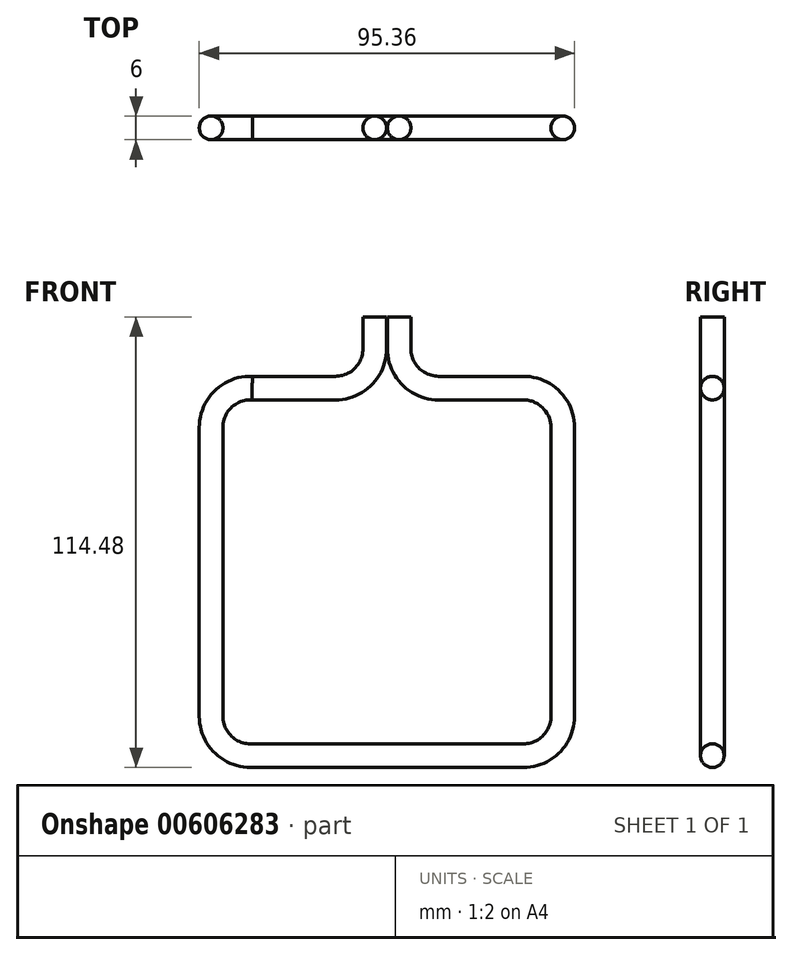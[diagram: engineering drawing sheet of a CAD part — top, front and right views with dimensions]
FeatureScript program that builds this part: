
annotation { "Feature Type Name" : "Feature", "Feature Type Description" : "" }
export const myFeature = defineFeature(function(context is Context, id is Id, definition is map)
    precondition{}
    {
        {
            var Q0;
            Q0=qCreatedBy(makeId("Front.planeOp"),FACE);
            var sketch = newSketch(context, id + "F0", { "sketchPlane" : qUnion([Q0])});
            skLineSegment(sketch, "E0.bottom", {"start": v(42, -43.5) * mm, "end": v(-42, -43.5) * mm});
            skLineSegment(sketch, "E0.top", {"start": v(42, 43.5) * mm, "end": v(-42, 43.5) * mm});
            skLineSegment(sketch, "E0.left", {"start": v(42, -43.5) * mm, "end": v(42, 43.5) * mm});
            skLineSegment(sketch, "E0.right", {"start": v(-42, -43.5) * mm, "end": v(-42, 43.5) * mm});
            skPoint(sketch, "E0.middle", {"position": v(0, 0) * mm});
            skLineSegment(sketch, "E1.bottom", {"start": v(34.68, -46.69) * mm, "end": v(-34.68, -46.69) * mm});
            skLineSegment(sketch, "E1.left", {"start": v(44.68, -36.69) * mm, "end": v(44.68, 36.69) * mm});
            skLineSegment(sketch, "E1.right", {"start": v(-44.68, -36.69) * mm, "end": v(-44.68, 36.69) * mm});
            skPoint(sketch, "E2.visualSharp", {"position": v(-44.68, 46.69) * mm});
            skArc(sketch, "E2.filletArc", {"start": v(-34.24, 46.68) * mm, "mid": v(-41.6, 43.91) * mm, "end": v(-44.68, 36.69) * mm});
            skPoint(sketch, "E3.visualSharp", {"position": v(44.68, 46.69) * mm});
            skArc(sketch, "E3.filletArc", {"start": v(44.68, 36.69) * mm, "mid": v(41.73, 43.78) * mm, "end": v(34.61, 46.69) * mm});
            skPoint(sketch, "E4.visualSharp", {"position": v(44.68, -46.69) * mm});
            skArc(sketch, "E4.filletArc", {"start": v(34.68, -46.69) * mm, "mid": v(41.75, -43.76) * mm, "end": v(44.68, -36.69) * mm});
            skPoint(sketch, "E5.visualSharp", {"position": v(-44.68, -46.69) * mm});
            skArc(sketch, "E5.filletArc", {"start": v(-44.68, -36.69) * mm, "mid": v(-41.75, -43.76) * mm, "end": v(-34.68, -46.69) * mm});
            skLineSegment(sketch, "E6.bottom", {"start": v(-34.24, 46.68) * mm, "end": v(-13.1, 46.68) * mm});
            skLineSegment(sketch, "E6.right", {"start": v(-3.1, 56.68) * mm, "end": v(-3.1, 64.79) * mm});
            skPoint(sketch, "E7.visualSharp", {"position": v(-3.1, 46.68) * mm});
            skArc(sketch, "E7.filletArc", {"start": v(-13.1, 46.68) * mm, "mid": v(-6.03, 49.6) * mm, "end": v(-3.1, 56.68) * mm});
            skLineSegment(sketch, "E8.bottom", {"start": v(34.61, 46.69) * mm, "end": v(13.1, 46.69) * mm});
            skLineSegment(sketch, "E8.right", {"start": v(3.1, 56.69) * mm, "end": v(3.1, 64.79) * mm});
            skPoint(sketch, "E9.visualSharp", {"position": v(3.1, 46.69) * mm});
            skArc(sketch, "E9.filletArc", {"start": v(3.1, 56.69) * mm, "mid": v(6.03, 49.62) * mm, "end": v(13.1, 46.69) * mm});
            skSolve(sketch);
        }
        {
            var Q0;
            Q0=qCreatedBy(makeId("Right.planeOp"),FACE);
            var sketch = newSketch(context, id + "F1", { "sketchPlane" : qUnion([Q0])});
            skCircle(sketch, "E10", {"center": v(0, -46.69) * mm, "radius": 3 * mm});
            skSolve(sketch);
        }
        {
            var Q0;
            Q0=makeQuery(id+"F1.imprint","IMPRINT",FACE,{"disambiguationData":[TD([[makeQuery(id+"F1.imprint","IMPRINT",EDGE,{"derivedFrom":sQuery(id+"F1.wireOp",EDGE,"E10")}),1.0]])]});
            var Q1;
            Q1=sQuery(id+"F0.wireOp",EDGE,"E1.bottom");
            var Q2;
            Q2=sQuery(id+"F0.wireOp",EDGE,"E4.filletArc");
            var Q3;
            Q3=sQuery(id+"F0.wireOp",EDGE,"E1.left");
            var Q4;
            Q4=sQuery(id+"F0.wireOp",EDGE,"E5.filletArc");
            var Q5;
            Q5=sQuery(id+"F0.wireOp",EDGE,"E1.right");
            var Q6;
            Q6=sQuery(id+"F0.wireOp",EDGE,"E2.filletArc");
            var Q7;
            Q7=sQuery(id+"F0.wireOp",EDGE,"E6.bottom");
            var Q8;
            Q8=sQuery(id+"F0.wireOp",EDGE,"E7.filletArc");
            var Q9;
            Q9=sQuery(id+"F0.wireOp",EDGE,"E6.right");
            var Q10;
            Q10=sQuery(id+"F0.wireOp",EDGE,"E8.right");
            var Q11;
            Q11=sQuery(id+"F0.wireOp",EDGE,"E9.filletArc");
            var Q12;
            Q12=sQuery(id+"F0.wireOp",EDGE,"E8.bottom");
            var Q13;
            Q13=sQuery(id+"F0.wireOp",EDGE,"E3.filletArc");
            sweep(context, id + "F2", {"profiles" : qUnion([Q0]), "path" : qUnion([Q1, Q2, Q3, Q4, Q5, Q6, Q7, Q8, Q9, Q10, Q11, Q12, Q13])});
        }
    });
